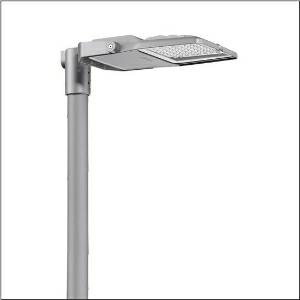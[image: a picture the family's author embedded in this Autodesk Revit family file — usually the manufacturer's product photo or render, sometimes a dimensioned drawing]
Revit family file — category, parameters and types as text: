
# Revit family: floodlight_fl_21_mini___pl64_5xa7776c2e3a_3ffb
name_source: partatom
category: Lighting Fixtures
units: mm (PartAtom-declared; Revit-internal decimal feet)

## family parameters
Cut with Voids When Loaded = No
Host = Face
Light Source = No
Part Type = Normal
Room Calculation Point = No
Round Connector Dimension = Use Diameter
Shared = No

## types (1)
- --- (1 x LED, 11770 lm, 89 W, 3000K)
    Apparent Load = 89 VA
    CIE Flux Codes = 28 80 98 100 100
    Color Rendering = 70
    Color Temperature = 3000K
    Default Elevation = 1800 mm
    Description = Floodlight FL 21 mini, floodlight, primary light control with lens, of PMMA, primary optical cover: protective disc, of toughened safety glass, transparent, light distribution: PL64, light emission: direct distribution, installation type: surface-mounted, LED, High Power LED, rated luminous flux: 11.770lm, luminous efficacy: 132lm/W, light colour: 730, colour temperature: 3000K, control gear: Smart Interface (Zhaga), control: flexible luminous flux parameterisation, time-dependent luminous flux control, constant luminous flux control, overheat protection, pre-setting: logarithmic dimming characteristic, with terminal, 6-pole, mains connection: 220..240V, AC, 50/60Hz, start of lifetime: 89W, end of service life: 94W, reduction: 43W, luminaire housing, of diecast aluminium, powder-coated, Siteco® metallic grey (DB 702S), corrosivity category C5 mid according to DIN EN ISO 12944, suitable for swimming pools, chlorine-resistant, sealing non-destructively replaceable, please order mast flange separately, mast bracket, of steel, galvanised, powder-coated, Siteco® metallic grey (DB 702S), Smart Interface below and above, protection rating (complete): IP66, insulation class (complete): insulation class II (safety insulation), certification: CE, ENEC, VDE, protection symbol: D, impact resistance: IK08, permissible operating ambient temperature: -40..+40°C, permissible operating ambient temperature for outdoor applications: -40..+50°C, standard: DIN EN 12944, LABS conformity tested according to VDMA 24364:2018-05, packaging unit: 1 piece

Light Distribution: PL64
    Height = 70 mm
    Lamp = 1 x LED
    Lamp Light Flux = 11770 lm
    Lamp Power = 89 W
    Lamp count = 1
    Length = 485 mm
    Luminous efficacy = 132 lm/W
    Manufacturer = Siteco
    ModVariant = No
    Model = 5XA7776C2E3A
    Number of Poles = 1
    OnlyDefault = Yes
    Power Factor = 1
    Product Name = Floodlight FL 21 mini | PL64
    Product group = floodlight | pylon annexe
    ProductGroupID = 6201
    Protection Class = Protection class II
    Protection Degree = IP 66
    RLX_Detail_Level = 1
    RLX_Emergency_Light_Flux = 0 lm
    RLX_Emergency_Type = 0
    RLX_Emergency_Type_DB = No
    RlxData = <blob elided: 101097 chars, md5=b0036202>
    Socket = socket
    Standby Power = 0 W
    System Light Flux = 11770 lm
    System Power = 89 W
    Type Comments = factory setting: luminous flux: 100 % | dim-lin: 254 | 456 mA
    Type Image = l_1007125.jpg
    URL = http://relux.com
    VarID = @adj_186805
    Voltage = 0 V
    Weight = 0.00 kg
    Width = 337 mm

## geometry (parser evidence)
native form markers: Blend x4, Sweep x13
no freeform markers — native parametric forms only
